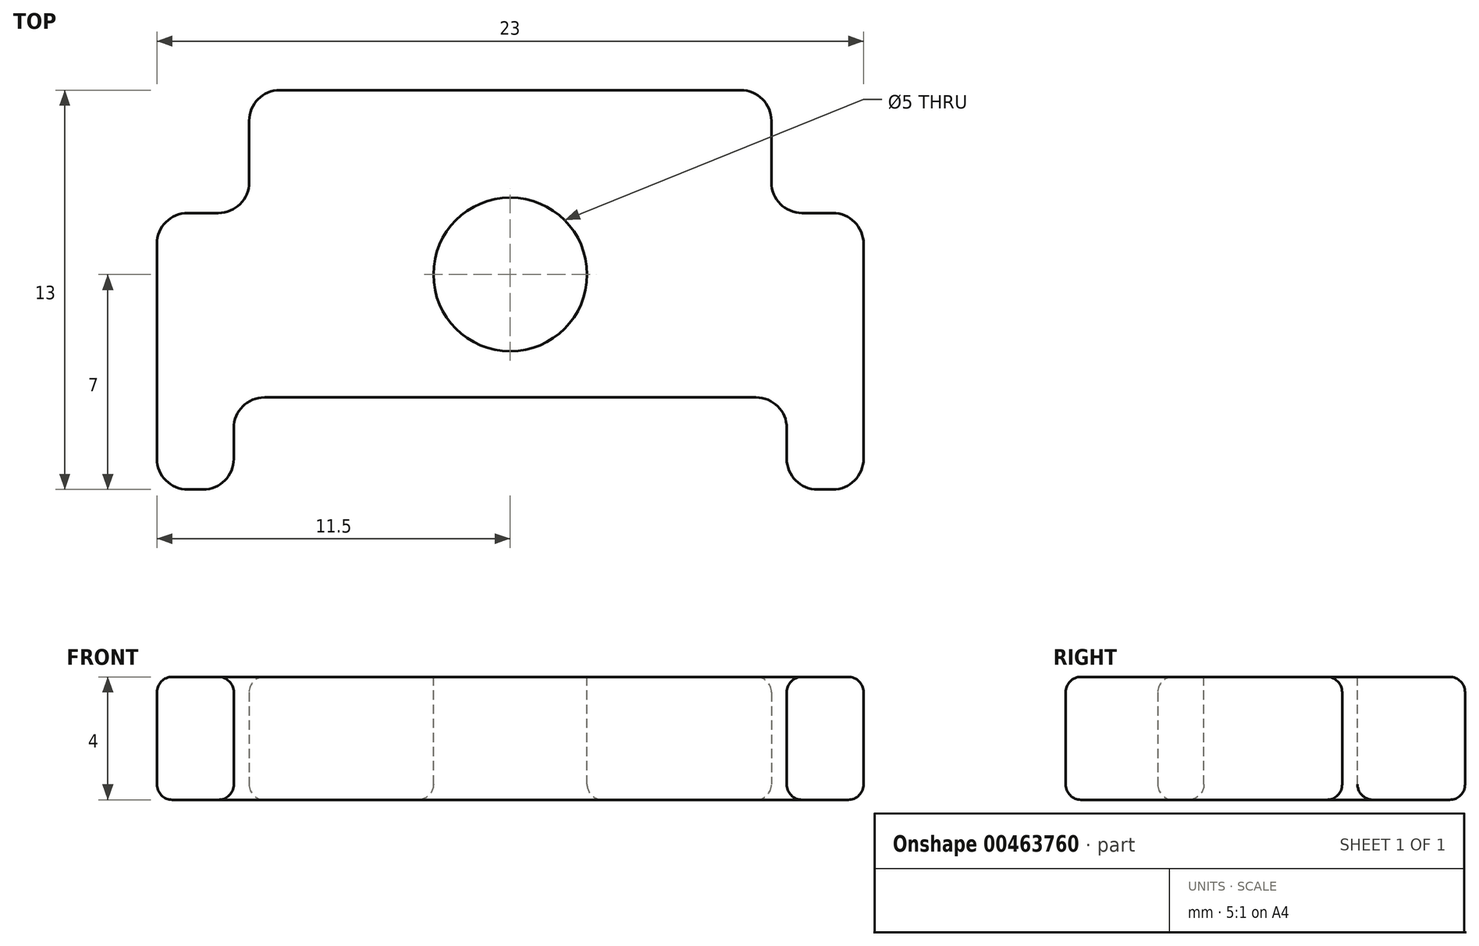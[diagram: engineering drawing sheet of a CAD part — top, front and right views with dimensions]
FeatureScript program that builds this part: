
annotation { "Feature Type Name" : "Feature", "Feature Type Description" : "" }
export const myFeature = defineFeature(function(context is Context, id is Id, definition is map)
    precondition{}
    {
        {
            var Q0;
            Q0=qCreatedBy(makeId("Top.planeOp"),FACE);
            var sketch = newSketch(context, id + "F0", { "sketchPlane" : qUnion([Q0])});
            skLineSegment(sketch, "E0", {"start": v(9, -13) * mm, "end": v(9, -10) * mm});
            skLineSegment(sketch, "E1", {"start": v(9, -10) * mm, "end": v(-9, -10) * mm});
            skLineSegment(sketch, "E2", {"start": v(-9, -10) * mm, "end": v(-9, -13) * mm});
            skLineSegment(sketch, "E3", {"start": v(-9, -13) * mm, "end": v(-11.5, -13) * mm});
            skLineSegment(sketch, "E4", {"start": v(9, -13) * mm, "end": v(11.5, -13) * mm});
            skLineSegment(sketch, "E5", {"start": v(-11.5, -13) * mm, "end": v(-11.5, -4) * mm});
            skLineSegment(sketch, "E6", {"start": v(-11.5, -4) * mm, "end": v(-8.5, -4) * mm});
            skLineSegment(sketch, "E7", {"start": v(-8.5, -4) * mm, "end": v(-8.5, 0) * mm});
            skLineSegment(sketch, "E8", {"start": v(-8.5, 0) * mm, "end": v(8.5, 0) * mm});
            skLineSegment(sketch, "E9", {"start": v(8.5, 0) * mm, "end": v(8.5, -4) * mm});
            skLineSegment(sketch, "E10", {"start": v(8.5, -4) * mm, "end": v(11.5, -4) * mm});
            skLineSegment(sketch, "E11", {"start": v(11.5, -4) * mm, "end": v(11.5, -13) * mm});
            skSolve(sketch);
        }
        {
            var Q0;
            Q0=makeQuery(id+"F0.imprint","IMPRINT",FACE,{"disambiguationData":[TD([[makeQuery(id+"F0.imprint","IMPRINT",EDGE,{"derivedFrom":sQuery(id+"F0.wireOp",EDGE,"E0")}),-1.0]])]});
            extrude(context, id + "F1", {"entities" : qUnion([Q0]), "depth" : 4 * mm});
        }
        {
            var Q0;
            Q0=makeQuery(id+"F1.opExtrude","SWEPT_EDGE",EDGE,{"disambiguationData":[OSD([sQuery(id+"F0.wireOp",EDGE,"JVpa2NSN-jCbz-SYZh-2br0-VPJ9OqO5sEDm"),sQuery(id+"F0.wireOp",EDGE,"TmuEh8Bb-qYGH-lmF9-es9h-PXmLGTj7apYS")])]});
            var Q1;
            Q1=makeQuery(id+"F1.opExtrude","SWEPT_EDGE",EDGE,{"disambiguationData":[OSD([sQuery(id+"F0.wireOp",EDGE,"Ta08JTOG-JjW1-DyQu-Rjfl-olB2hLuTZKrI"),sQuery(id+"F0.wireOp",EDGE,"5RLxsvr7-zWRq-nJ0O-23qe-XEgADmnkmLba")])]});
            var Q2;
            Q2=makeQuery(id+"F1.opExtrude","SWEPT_EDGE",EDGE,{"disambiguationData":[OSD([sQuery(id+"F0.wireOp",EDGE,"JVpa2NSN-jCbz-SYZh-2br0-VPJ9OqO5sEDm"),sQuery(id+"F0.wireOp",EDGE,"iIMMWLLX-5pRk-kAWc-YyXh-X3XYjQtiHgF8")])]});
            var Q3;
            Q3=makeQuery(id+"F1.opExtrude","SWEPT_EDGE",EDGE,{"disambiguationData":[OSD([sQuery(id+"F0.wireOp",EDGE,"Bp2VUUx9-f2Nf-Cqm2-FavC-f2X54JljXIIN"),sQuery(id+"F0.wireOp",EDGE,"TmuEh8Bb-qYGH-lmF9-es9h-PXmLGTj7apYS")])]});
            var Q4;
            Q4=makeQuery(id+"F1.opExtrude","SWEPT_EDGE",EDGE,{"disambiguationData":[OSD([sQuery(id+"F0.wireOp",EDGE,"aM0JYdi9-BpOH-c1Sx-eQZ7-4LdQcpM627Qa"),sQuery(id+"F0.wireOp",EDGE,"Ta08JTOG-JjW1-DyQu-Rjfl-olB2hLuTZKrI")])]});
            var Q5;
            Q5=makeQuery(id+"F1.opExtrude","SWEPT_EDGE",EDGE,{"disambiguationData":[OSD([sQuery(id+"F0.wireOp",EDGE,"5RLxsvr7-zWRq-nJ0O-23qe-XEgADmnkmLba"),sQuery(id+"F0.wireOp",EDGE,"Bp2VUUx9-f2Nf-Cqm2-FavC-f2X54JljXIIN")])]});
            var Q6;
            Q6=makeQuery(id+"F1.opExtrude","SWEPT_EDGE",EDGE,{"disambiguationData":[OSD([sQuery(id+"F0.wireOp",EDGE,"yeDMJLls-6pq1-5wso-vwFU-Q73Pk40JU32b"),sQuery(id+"F0.wireOp",EDGE,"aM0JYdi9-BpOH-c1Sx-eQZ7-4LdQcpM627Qa")])]});
            var Q7;
            Q7=makeQuery(id+"F1.opExtrude","SWEPT_EDGE",EDGE,{"disambiguationData":[OSD([sQuery(id+"F0.wireOp",EDGE,"yeDMJLls-6pq1-5wso-vwFU-Q73Pk40JU32b"),sQuery(id+"F0.wireOp",EDGE,"oADVPvip-QRiO-k2je-1GcM-0gCGYZzCVpqe")])]});
            var Q8;
            Q8=makeQuery(id+"F1.opExtrude","SWEPT_EDGE",EDGE,{"disambiguationData":[OSD([sQuery(id+"F0.wireOp",EDGE,"oADVPvip-QRiO-k2je-1GcM-0gCGYZzCVpqe"),sQuery(id+"F0.wireOp",EDGE,"10rlgXVg-n50c-kqx7-uExC-2RYqwfv1c7cX")])]});
            var Q9;
            Q9=makeQuery(id+"F1.opExtrude","SWEPT_EDGE",EDGE,{"disambiguationData":[OSD([sQuery(id+"F0.wireOp",EDGE,"TUznSBm0-cCe5-ovrQ-pSbA-vPagOil4q95r"),sQuery(id+"F0.wireOp",EDGE,"10rlgXVg-n50c-kqx7-uExC-2RYqwfv1c7cX")])]});
            var Q10;
            Q10=makeQuery(id+"F1.opExtrude","SWEPT_EDGE",EDGE,{"disambiguationData":[OSD([sQuery(id+"F0.wireOp",EDGE,"dIuJsfEi-w8Eu-UMFV-xWrQ-Q2fZL97E1xqK"),sQuery(id+"F0.wireOp",EDGE,"TUznSBm0-cCe5-ovrQ-pSbA-vPagOil4q95r")])]});
            var Q11;
            Q11=makeQuery(id+"F1.opExtrude","SWEPT_EDGE",EDGE,{"disambiguationData":[OSD([sQuery(id+"F0.wireOp",EDGE,"iIMMWLLX-5pRk-kAWc-YyXh-X3XYjQtiHgF8"),sQuery(id+"F0.wireOp",EDGE,"dIuJsfEi-w8Eu-UMFV-xWrQ-Q2fZL97E1xqK")])]});
            var Q12;
            Q12=makeQuery(id+"F1.opExtrude","SWEPT_EDGE",EDGE,{"disambiguationData":[OSD([sQuery(id+"F0.wireOp",EDGE,"yLF3BCVI-Jb2U-5dZP-aiB0-7200LCA53yiJ"),sQuery(id+"F0.wireOp",EDGE,"E3")])]});
            var Q13;
            Q13=makeQuery(id+"F1.opExtrude","SWEPT_EDGE",EDGE,{"disambiguationData":[OSD([sQuery(id+"F0.wireOp",EDGE,"E2"),sQuery(id+"F0.wireOp",EDGE,"E3")])]});
            var Q14;
            Q14=makeQuery(id+"F1.opExtrude","SWEPT_EDGE",EDGE,{"disambiguationData":[OSD([sQuery(id+"F0.wireOp",EDGE,"E1"),sQuery(id+"F0.wireOp",EDGE,"E2")])]});
            var Q15;
            Q15=makeQuery(id+"F1.opExtrude","SWEPT_EDGE",EDGE,{"disambiguationData":[OSD([sQuery(id+"F0.wireOp",EDGE,"E0"),sQuery(id+"F0.wireOp",EDGE,"E1")])]});
            var Q16;
            Q16=makeQuery(id+"F1.opExtrude","SWEPT_EDGE",EDGE,{"disambiguationData":[OSD([sQuery(id+"F0.wireOp",EDGE,"E0"),sQuery(id+"F0.wireOp",EDGE,"E4")])]});
            var Q17;
            Q17=makeQuery(id+"F1.opExtrude","SWEPT_EDGE",EDGE,{"disambiguationData":[OSD([sQuery(id+"F0.wireOp",EDGE,"W0sLsfjq-YAJu-qSV0-cM3q-n6XLMPe2tytr"),sQuery(id+"F0.wireOp",EDGE,"E4")])]});
            var Q18;
            Q18=makeQuery(id+"F1.opExtrude","SWEPT_EDGE",EDGE,{"disambiguationData":[OSD([sQuery(id+"F0.wireOp",EDGE,"E5"),sQuery(id+"F0.wireOp",EDGE,"E6")])]});
            var Q19;
            Q19=makeQuery(id+"F1.opExtrude","SWEPT_EDGE",EDGE,{"disambiguationData":[OSD([sQuery(id+"F0.wireOp",EDGE,"E6"),sQuery(id+"F0.wireOp",EDGE,"E7")])]});
            var Q20;
            Q20=makeQuery(id+"F1.opExtrude","SWEPT_EDGE",EDGE,{"disambiguationData":[OSD([sQuery(id+"F0.wireOp",EDGE,"E7"),sQuery(id+"F0.wireOp",EDGE,"E8")])]});
            var Q21;
            Q21=makeQuery(id+"F1.opExtrude","SWEPT_EDGE",EDGE,{"disambiguationData":[OSD([sQuery(id+"F0.wireOp",EDGE,"E8"),sQuery(id+"F0.wireOp",EDGE,"E9")])]});
            var Q22;
            Q22=makeQuery(id+"F1.opExtrude","SWEPT_EDGE",EDGE,{"disambiguationData":[OSD([sQuery(id+"F0.wireOp",EDGE,"E9"),sQuery(id+"F0.wireOp",EDGE,"E10")])]});
            var Q23;
            Q23=makeQuery(id+"F1.opExtrude","SWEPT_EDGE",EDGE,{"disambiguationData":[OSD([sQuery(id+"F0.wireOp",EDGE,"E10"),sQuery(id+"F0.wireOp",EDGE,"E11")])]});
            fillet(context, id + "F2", {"entities" : qUnion([Q0, Q1, Q2, Q3, Q4, Q5, Q6, Q7, Q8, Q9, Q10, Q11, Q12, Q13, Q14, Q15, Q16, Q17, Q18, Q19, Q20, Q21, Q22, Q23]), "radius" : 1 * mm, "tangentPropagation" : true, "allowEdgeOverflow" : false});
        }
        {
            var Q0;
            Q0=makeQuery(id+"F1.opExtrude","CAP_EDGE",EDGE,{"disambiguationData":[OSD([sQuery(id+"F0.wireOp",EDGE,"10rlgXVg-n50c-kqx7-uExC-2RYqwfv1c7cX")])],"isStart":false});
            var Q1;
            Q1=makeQuery(id+"F1.opExtrude","CAP_EDGE",EDGE,{"disambiguationData":[OSD([sQuery(id+"F0.wireOp",EDGE,"TUznSBm0-cCe5-ovrQ-pSbA-vPagOil4q95r")])],"isStart":true});
            var Q2;
            Q2=makeQuery(id+"F1.opExtrude","CAP_EDGE",EDGE,{"disambiguationData":[OSD([sQuery(id+"F0.wireOp",EDGE,"E1")])],"isStart":false});
            var Q3;
            Q3=makeQuery(id+"F1.opExtrude","CAP_EDGE",EDGE,{"disambiguationData":[OSD([sQuery(id+"F0.wireOp",EDGE,"E2")])],"isStart":false});
            var Q4;
            Q4=makeQuery(id+"F1.opExtrude","CAP_FACE",FACE,{"disambiguationData":[OSD([sQuery(id+"F0.wireOp",EDGE,"yeDMJLls-6pq1-5wso-vwFU-Q73Pk40JU32b"),sQuery(id+"F0.wireOp",EDGE,"dIuJsfEi-w8Eu-UMFV-xWrQ-Q2fZL97E1xqK"),sQuery(id+"F0.wireOp",EDGE,"TUznSBm0-cCe5-ovrQ-pSbA-vPagOil4q95r"),sQuery(id+"F0.wireOp",EDGE,"oADVPvip-QRiO-k2je-1GcM-0gCGYZzCVpqe"),sQuery(id+"F0.wireOp",EDGE,"10rlgXVg-n50c-kqx7-uExC-2RYqwfv1c7cX"),sQuery(id+"F0.wireOp",EDGE,"yLF3BCVI-Jb2U-5dZP-aiB0-7200LCA53yiJ"),sQuery(id+"F0.wireOp",EDGE,"W0sLsfjq-YAJu-qSV0-cM3q-n6XLMPe2tytr"),sQuery(id+"F0.wireOp",EDGE,"E0"),sQuery(id+"F0.wireOp",EDGE,"E1"),sQuery(id+"F0.wireOp",EDGE,"E2"),sQuery(id+"F0.wireOp",EDGE,"E3"),sQuery(id+"F0.wireOp",EDGE,"E4")])],"isStart":false});
            var Q5;
            Q5=makeQuery(id+"F1.opExtrude","CAP_EDGE",EDGE,{"disambiguationData":[OSD([sQuery(id+"F0.wireOp",EDGE,"E1")])],"isStart":true});
            var Q6;
            Q6=makeQuery(id+"F1.opExtrude","CAP_EDGE",EDGE,{"disambiguationData":[OSD([sQuery(id+"F0.wireOp",EDGE,"E4")])],"isStart":true});
            var Q7;
            Q7=makeQuery(id+"F1.opExtrude","CAP_EDGE",EDGE,{"disambiguationData":[OSD([sQuery(id+"F0.wireOp",EDGE,"E0")])],"isStart":true});
            var Q8;
            Q8=makeQuery(id+"F1.opExtrude","CAP_EDGE",EDGE,{"disambiguationData":[OSD([sQuery(id+"F0.wireOp",EDGE,"E2")])],"isStart":true});
            var Q9;
            Q9=makeQuery(id+"F1.opExtrude","CAP_EDGE",EDGE,{"disambiguationData":[OSD([sQuery(id+"F0.wireOp",EDGE,"E3")])],"isStart":true});
            fillet(context, id + "F3", {"entities" : qUnion([Q0, Q1, Q2, Q3, Q4, Q5, Q6, Q7, Q8, Q9]), "radius" : 0.5 * mm, "tangentPropagation" : true, "allowEdgeOverflow" : false});
        }
        {
            var Q0;
            Q0=makeQuery(id+"F1.opExtrude","CAP_FACE",FACE,{"disambiguationData":[OSD([sQuery(id+"F0.wireOp",EDGE,"E0"),sQuery(id+"F0.wireOp",EDGE,"E1"),sQuery(id+"F0.wireOp",EDGE,"E2"),sQuery(id+"F0.wireOp",EDGE,"E3"),sQuery(id+"F0.wireOp",EDGE,"E4"),sQuery(id+"F0.wireOp",EDGE,"E5"),sQuery(id+"F0.wireOp",EDGE,"E6"),sQuery(id+"F0.wireOp",EDGE,"E7"),sQuery(id+"F0.wireOp",EDGE,"E8"),sQuery(id+"F0.wireOp",EDGE,"E9"),sQuery(id+"F0.wireOp",EDGE,"E10"),sQuery(id+"F0.wireOp",EDGE,"E11")])],"isStart":false});
            var sketch = newSketch(context, id + "F4", { "sketchPlane" : qUnion([Q0])});
            skLineSegment(sketch, "E12", {"start": v(0, 0) * mm, "end": v(0, -6) * mm});
            skPoint(sketch, "E12.endSnap0", {"position": v(0, -0.5) * mm});
            skCircle(sketch, "E13", {"center": v(0, -6) * mm, "radius": 2.5 * mm});
            skSolve(sketch);
        }
        {
            var Q0;
            Q0=makeQuery(id+"F4.imprint","IMPRINT",FACE,{"disambiguationData":[TD([[makeQuery(id+"F4.imprint","IMPRINT",EDGE,{"derivedFrom":sQuery(id+"F4.wireOp",EDGE,"E13")}),1.0]])]});
            extrude(context, id + "F5", {"entities" : qUnion([Q0]), "operationType" : NewBodyOperationType.REMOVE, "endBound" : BoundingType.THROUGH_ALL, "oppositeDirection" : true, "depth" : 25 * mm});
        }
        {
            var Q0;
            Q0=makeQuery(id+"F5.boolean.opBoolean","COPY",EDGE,{"derivedFrom":makeQuery(id+"F5.opExtrude","CAP_EDGE",EDGE,{"disambiguationData":[OSD([sQuery(id+"F4.wireOp",EDGE,"E13")])],"isStart":true})});
            var Q1;
            Q1=makeQuery(id+"F5.boolean.opBoolean","INTERSECT",EDGE,{"derivedFrom":[makeQuery(id+"F1.opExtrude","CAP_FACE",FACE,{"disambiguationData":[OSD([sQuery(id+"F0.wireOp",EDGE,"E0"),sQuery(id+"F0.wireOp",EDGE,"E1"),sQuery(id+"F0.wireOp",EDGE,"E2"),sQuery(id+"F0.wireOp",EDGE,"E3"),sQuery(id+"F0.wireOp",EDGE,"E4"),sQuery(id+"F0.wireOp",EDGE,"E5"),sQuery(id+"F0.wireOp",EDGE,"E6"),sQuery(id+"F0.wireOp",EDGE,"E7"),sQuery(id+"F0.wireOp",EDGE,"E8"),sQuery(id+"F0.wireOp",EDGE,"E9"),sQuery(id+"F0.wireOp",EDGE,"E10"),sQuery(id+"F0.wireOp",EDGE,"E11")])],"isStart":true}),makeQuery(id+"F5.opExtrude","SWEPT_FACE",FACE,{"disambiguationData":[OSD([sQuery(id+"F4.wireOp",EDGE,"E13")])]})]});
            fillet(context, id + "F6", {"entities" : qUnion([Q0, Q1]), "radius" : 0.5 * mm, "tangentPropagation" : true, "allowEdgeOverflow" : false});
        }
    });
